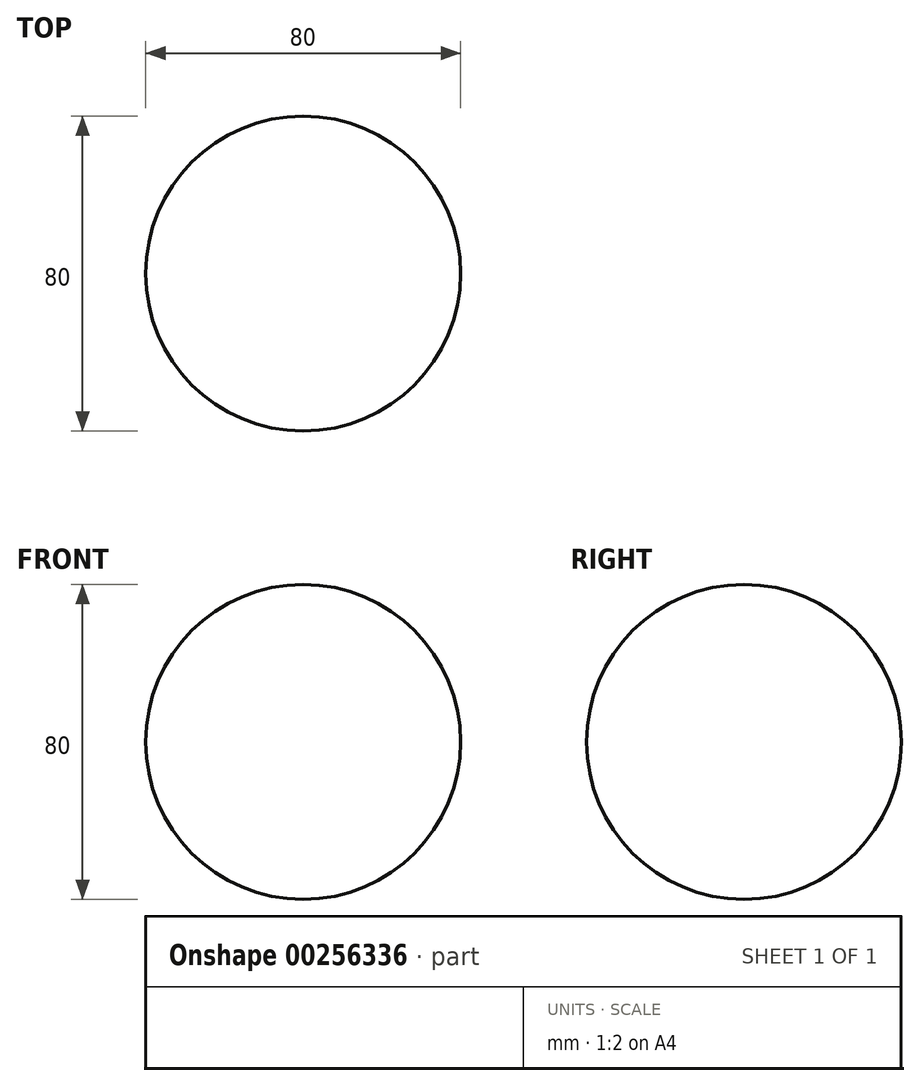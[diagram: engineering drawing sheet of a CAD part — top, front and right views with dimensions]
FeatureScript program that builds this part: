
annotation { "Feature Type Name" : "Feature", "Feature Type Description" : "" }
export const myFeature = defineFeature(function(context is Context, id is Id, definition is map)
    precondition{}
    {
        {
            var Q0;
            Q0=qCreatedBy(makeId("Front.planeOp"),FACE);
            var sketch = newSketch(context, id + "F0", { "sketchPlane" : qUnion([Q0])});
            skArc(sketch, "E0", {"start": v(0, 40) * mm, "mid": v(40, 0) * mm, "end": v(0, -40) * mm});
            skLineSegment(sketch, "E1", {"start": v(0, 40) * mm, "end": v(0, -40) * mm});
            skLineSegment(sketch, "E2", {"start": v(0, -55.11) * mm, "end": v(0, 50.86) * mm, "construction": true});
            skSolve(sketch);
        }
        {
            var Q0;
            Q0 = qSketchRegion(id + "F0", true);
            var Q1;
            Q1=sQuery(id+"F0.wireOp",EDGE,"E2");
            revolve(context, id + "F1", {"entities" : qUnion([Q0]), "axis" : qUnion([Q1]), "revolveType" : RevolveType.FULL});
        }
    });
